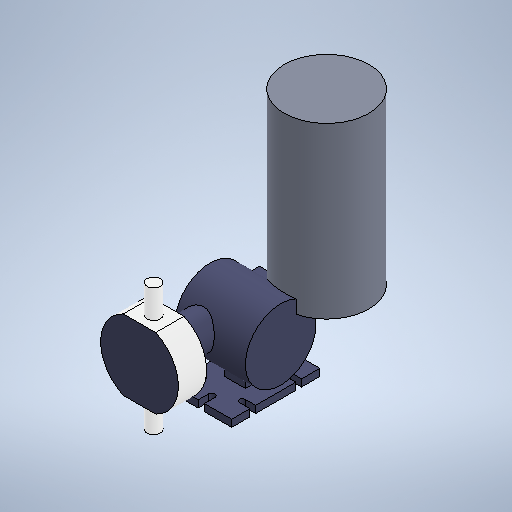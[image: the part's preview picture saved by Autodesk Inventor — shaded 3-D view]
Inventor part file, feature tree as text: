
AUTODESK INVENTOR PART (.ipt)
format: ipt  version: 2025 (Build 290162010, 162A)  size: 355,328 bytes
history: native  units: mm
features: extrude x7, sketch x7, plane x1
ambient origin geometry x8: Origin, YZ Plane, XZ Plane, XY Plane, X Axis, Y Axis, Z Axis, Center Point
bodies: Solid1 (feature_tree)
feature tree (15):
  extrude  "Extrusion1"  Depth=125.0mm
  extrude  "Extrusion2"  Depth=65.0mm
  extrude  "Extrusion3"  Depth=4.5mm
  extrude  "Extrusion4"  Depth=10.0mm TaperAngle=0.0deg
  extrude  "Extrusion5"  Depth=50.0mm
  extrude  "Extrusion6"  Depth=120.0mm TaperAngle=0.0deg
  plane  "Work Plane1"
  extrude  "Extrusion7"  Depth=100.0mm
  sketch  "Sketch1"  dims[d0=86.0mm d1=125.0mm]
  sketch  "Sketch3"  dims[d2=4.0mm d3=65.0mm]
  sketch  "Sketch4"  dims[d4=15.0mm d5=4.5mm]
  sketch  "Sketch5"  dims[d6=15.0mm d7=10.0mm d8=0.0mm]
  sketch  "Sketch6"  dims[d9=30.0mm d10=50.0mm]
  sketch  "Sketch7"  dims[d11=15.0mm d12=120.0mm d13=0.0mm]
  sketch  "Sketch8"  dims[d14=94.0mm d15=100.0mm d16=20.0mm d17=70.0mm d18=30.0mm d19=0.0mm d20=0.0mm d21=120.0mm d22=55.0mm d23=60.0mm d24=240.0mm d25=0.0mm d26=50.0mm d27=100.0mm d28=150.0mm d29=0.0mm d30=110.0mm d31=100.0mm d32=40.0mm d33=0.0mm d34=100.0mm d35=19.05mm d36=130.0mm d37=180.0mm d38=0.0mm]
